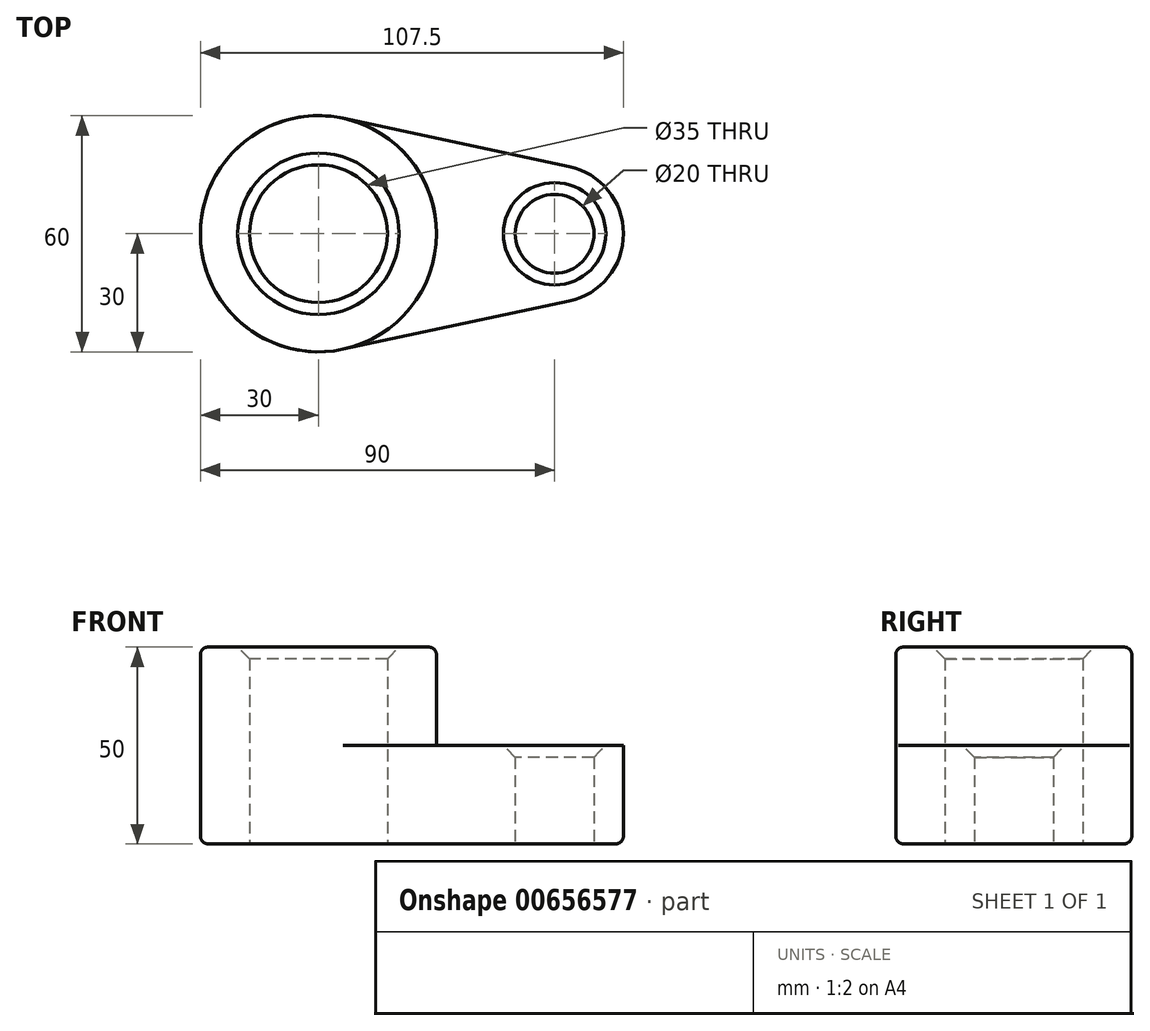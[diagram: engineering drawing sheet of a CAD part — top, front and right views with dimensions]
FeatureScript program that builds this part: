
annotation { "Feature Type Name" : "Feature", "Feature Type Description" : "" }
export const myFeature = defineFeature(function(context is Context, id is Id, definition is map)
    precondition{}
    {
        {
            var Q0;
            Q0=qCreatedBy(makeId("Top.planeOp"),FACE);
            var sketch = newSketch(context, id + "F0", { "sketchPlane" : qUnion([Q0])});
            skCircle(sketch, "E0", {"center": v(0, 0) * mm, "radius": 30 * mm});
            skCircle(sketch, "E1", {"center": v(60, 0) * mm, "radius": 17.5 * mm});
            skLineSegment(sketch, "E2", {"start": v(6.25, 29.34) * mm, "end": v(63.65, 17.12) * mm});
            skLineSegment(sketch, "E3", {"start": v(6.25, -29.34) * mm, "end": v(63.65, -17.12) * mm});
            skCircle(sketch, "E4", {"center": v(0, 0) * mm, "radius": 17.5 * mm});
            skCircle(sketch, "E5", {"center": v(60, 0) * mm, "radius": 10 * mm});
            skSolve(sketch);
        }
        {
            var Q0;
            Q0 = qSketchRegion(id + "F0", true);
            extrude(context, id + "F1", {"entities" : qUnion([Q0]), "depth" : 25 * mm, "offsetDistance" : 25 * mm});
        }
        {
            var Q0;
            Q0=makeQuery(id+"F0.imprint","IMPRINT",FACE,{"disambiguationData":[TD([[makeQuery(id+"F0.imprint","IMPRINT",EDGE,{"derivedFrom":sQuery(id+"F0.wireOp",EDGE,"E4")}),-1.0]])]});
            extrude(context, id + "F2", {"entities" : qUnion([Q0]), "operationType" : NewBodyOperationType.ADD, "depth" : 50 * mm, "offsetDistance" : 25 * mm});
        }
        {
            var Q0;
            Q0=makeQuery(id+"F2.opExtrude","CAP_EDGE",EDGE,{"disambiguationData":[OSD([sQuery(id+"F0.wireOp",EDGE,"E0")])],"isStart":false});
            var Q1;
            Q1=makeQuery(id+"F1.opExtrude","CAP_EDGE",EDGE,{"disambiguationData":[OSD([sQuery(id+"F0.wireOp",EDGE,"E3")])],"isStart":true});
            var Q2;
            Q2=makeQuery(id+"F1.opExtrude","CAP_EDGE",EDGE,{"disambiguationData":[OSD([sQuery(id+"F0.wireOp",EDGE,"E2")])],"isStart":true});
            fillet(context, id + "F3", {"entities" : qUnion([Q0, Q1, Q2]), "radius" : 2 * mm, "tangentPropagation" : true, "allowEdgeOverflow" : false});
        }
        {
            var Q0;
            Q0=makeQuery(id+"F2.opExtrude","CAP_EDGE",EDGE,{"disambiguationData":[OSD([sQuery(id+"F0.wireOp",EDGE,"E4")])],"isStart":false});
            var Q1;
            Q1=makeQuery(id+"F1.opExtrude","CAP_EDGE",EDGE,{"disambiguationData":[OSD([sQuery(id+"F0.wireOp",EDGE,"E5")])],"isStart":false});
            chamfer(context, id + "F4", {"entities" : qUnion([Q0, Q1]), "width" : 3 * mm, "tangentPropagation" : true});
        }
    });
